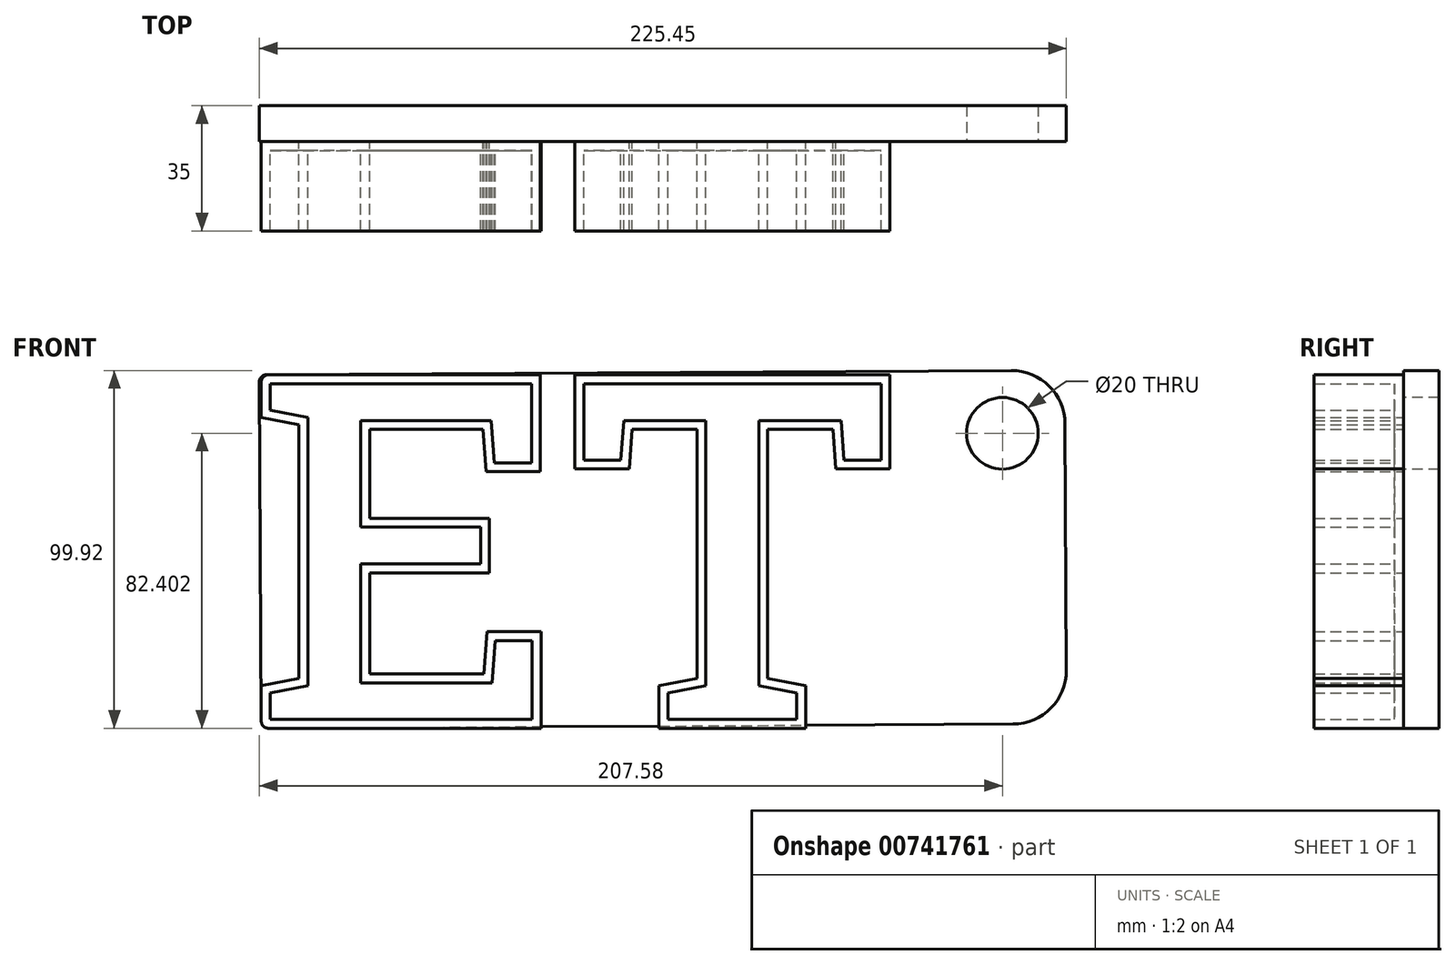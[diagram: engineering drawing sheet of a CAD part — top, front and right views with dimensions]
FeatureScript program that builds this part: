
annotation { "Feature Type Name" : "Feature", "Feature Type Description" : "" }
export const myFeature = defineFeature(function(context is Context, id is Id, definition is map)
    precondition{}
    {
        {
            var Q0;
            Q0=qCreatedBy(makeId("Front.planeOp"),FACE);
            var sketch = newSketch(context, id + "F0", { "sketchPlane" : qUnion([Q0])});
            skText(sketch, "E0", { "text": "ET", "fontName": "RobotoSlab-Bold.ttf"});
            const initialGuessF0  = {"E0": [0, -0.1, 1, 0, 0.1]};
            skSetInitialGuess(sketch, initialGuessF0);
            skSolve(sketch);
        }
        {
            var Q0;
            Q0 = qSketchRegion(id + "F0", true);
            extrude(context, id + "F1", {"entities" : qUnion([Q0]), "depth" : 25 * mm, "offsetDistance" : 25 * mm});
        }
        {
            var Q0;
            Q0=makeQuery(id+"F1.opExtrude","CAP_FACE",FACE,{"disambiguationData":[OSD([sQuery(id+"F0.wireOp",EDGE,"E0.sketch_text.stroke-0"),sQuery(id+"F0.wireOp",EDGE,"E0.sketch_text.stroke-1"),sQuery(id+"F0.wireOp",EDGE,"E0.sketch_text.stroke-2"),sQuery(id+"F0.wireOp",EDGE,"E0.sketch_text.stroke-3"),sQuery(id+"F0.wireOp",EDGE,"E0.sketch_text.stroke-4"),sQuery(id+"F0.wireOp",EDGE,"E0.sketch_text.stroke-5"),sQuery(id+"F0.wireOp",EDGE,"E0.sketch_text.stroke-6"),sQuery(id+"F0.wireOp",EDGE,"E0.sketch_text.stroke-7"),sQuery(id+"F0.wireOp",EDGE,"E0.sketch_text.stroke-8"),sQuery(id+"F0.wireOp",EDGE,"E0.sketch_text.stroke-9"),sQuery(id+"F0.wireOp",EDGE,"E0.sketch_text.stroke-10"),sQuery(id+"F0.wireOp",EDGE,"E0.sketch_text.stroke-11"),sQuery(id+"F0.wireOp",EDGE,"E0.sketch_text.stroke-12"),sQuery(id+"F0.wireOp",EDGE,"E0.sketch_text.stroke-13"),sQuery(id+"F0.wireOp",EDGE,"E0.sketch_text.stroke-14"),sQuery(id+"F0.wireOp",EDGE,"E0.sketch_text.stroke-15"),sQuery(id+"F0.wireOp",EDGE,"E0.sketch_text.stroke-16"),sQuery(id+"F0.wireOp",EDGE,"E0.sketch_text.stroke-17"),sQuery(id+"F0.wireOp",EDGE,"E0.sketch_text.stroke-18"),sQuery(id+"F0.wireOp",EDGE,"E0.sketch_text.stroke-19"),sQuery(id+"F0.wireOp",EDGE,"E0.sketch_text.stroke-20")])],"isStart":false});
            var Q1;
            Q1=makeQuery(id+"F1.opExtrude","CAP_FACE",FACE,{"disambiguationData":[OSD([sQuery(id+"F0.wireOp",EDGE,"E0.sketch_text.stroke-21"),sQuery(id+"F0.wireOp",EDGE,"E0.sketch_text.stroke-22"),sQuery(id+"F0.wireOp",EDGE,"E0.sketch_text.stroke-23"),sQuery(id+"F0.wireOp",EDGE,"E0.sketch_text.stroke-24"),sQuery(id+"F0.wireOp",EDGE,"E0.sketch_text.stroke-25"),sQuery(id+"F0.wireOp",EDGE,"E0.sketch_text.stroke-26"),sQuery(id+"F0.wireOp",EDGE,"E0.sketch_text.stroke-27"),sQuery(id+"F0.wireOp",EDGE,"E0.sketch_text.stroke-28"),sQuery(id+"F0.wireOp",EDGE,"E0.sketch_text.stroke-29"),sQuery(id+"F0.wireOp",EDGE,"E0.sketch_text.stroke-30"),sQuery(id+"F0.wireOp",EDGE,"E0.sketch_text.stroke-31"),sQuery(id+"F0.wireOp",EDGE,"E0.sketch_text.stroke-32"),sQuery(id+"F0.wireOp",EDGE,"E0.sketch_text.stroke-33"),sQuery(id+"F0.wireOp",EDGE,"E0.sketch_text.stroke-34"),sQuery(id+"F0.wireOp",EDGE,"E0.sketch_text.stroke-35"),sQuery(id+"F0.wireOp",EDGE,"E0.sketch_text.stroke-36")])],"isStart":false});
            shell(context, id + "F2", {"entities" : qUnion([Q0, Q1]), "thickness" : 2.5 * mm});
        }
        {
            var Q0;
            Q0=makeQuery(id+"F1.opExtrude","CAP_FACE",FACE,{"disambiguationData":[OSD([sQuery(id+"F0.wireOp",EDGE,"E0.sketch_text.stroke-0"),sQuery(id+"F0.wireOp",EDGE,"E0.sketch_text.stroke-1"),sQuery(id+"F0.wireOp",EDGE,"E0.sketch_text.stroke-2"),sQuery(id+"F0.wireOp",EDGE,"E0.sketch_text.stroke-3"),sQuery(id+"F0.wireOp",EDGE,"E0.sketch_text.stroke-4"),sQuery(id+"F0.wireOp",EDGE,"E0.sketch_text.stroke-5"),sQuery(id+"F0.wireOp",EDGE,"E0.sketch_text.stroke-6"),sQuery(id+"F0.wireOp",EDGE,"E0.sketch_text.stroke-7"),sQuery(id+"F0.wireOp",EDGE,"E0.sketch_text.stroke-8"),sQuery(id+"F0.wireOp",EDGE,"E0.sketch_text.stroke-9"),sQuery(id+"F0.wireOp",EDGE,"E0.sketch_text.stroke-10"),sQuery(id+"F0.wireOp",EDGE,"E0.sketch_text.stroke-11"),sQuery(id+"F0.wireOp",EDGE,"E0.sketch_text.stroke-12"),sQuery(id+"F0.wireOp",EDGE,"E0.sketch_text.stroke-13"),sQuery(id+"F0.wireOp",EDGE,"E0.sketch_text.stroke-14"),sQuery(id+"F0.wireOp",EDGE,"E0.sketch_text.stroke-15"),sQuery(id+"F0.wireOp",EDGE,"E0.sketch_text.stroke-16"),sQuery(id+"F0.wireOp",EDGE,"E0.sketch_text.stroke-17"),sQuery(id+"F0.wireOp",EDGE,"E0.sketch_text.stroke-18"),sQuery(id+"F0.wireOp",EDGE,"E0.sketch_text.stroke-19"),sQuery(id+"F0.wireOp",EDGE,"E0.sketch_text.stroke-20")])],"isStart":true});
            var sketch = newSketch(context, id + "F3", { "sketchPlane" : qUnion([Q0])});
            skLineSegment(sketch, "E1.bottom", {"start": v(-3.8, -100) * mm, "end": v(-228.8, -98.74) * mm});
            skLineSegment(sketch, "E1.top", {"start": v(-3.25, -1.26) * mm, "end": v(-228.24, 0) * mm});
            skLineSegment(sketch, "E1.left", {"start": v(-3.8, -100) * mm, "end": v(-3.25, -1.26) * mm});
            skLineSegment(sketch, "E1.right", {"start": v(-228.8, -98.74) * mm, "end": v(-228.24, 0) * mm});
            skSolve(sketch);
        }
        {
            var Q0;
            Q0 = qSketchRegion(id + "F3", true);
            extrude(context, id + "F4", {"entities" : qUnion([Q0]), "depth" : 10 * mm, "offsetDistance" : 25 * mm});
        }
        {
            var Q0;
            Q0=makeQuery(id+"F4.opExtrude","CAP_FACE",FACE,{"disambiguationData":[OSD([sQuery(id+"F3.wireOp",EDGE,"E1.bottom"),sQuery(id+"F3.wireOp",EDGE,"E1.top"),sQuery(id+"F3.wireOp",EDGE,"E1.left"),sQuery(id+"F3.wireOp",EDGE,"E1.right")])],"isStart":true});
            var sketch = newSketch(context, id + "F5", { "sketchPlane" : qUnion([Q0])});
            skPoint(sketch, "E2", {"position": v(210.84, -17.6) * mm});
            skSolve(sketch);
        }
        {
            var Q0;
            Q0=sQuery(id+"F5.wireOp",VERTEX,"E2");
            var Q1;
            Q1=makeQuery(id+"F4.opExtrude","SWEPT_BODY",BODY,{"disambiguationData":[OSD([sQuery(id+"F3.wireOp",EDGE,"E1.bottom"),sQuery(id+"F3.wireOp",EDGE,"E1.top"),sQuery(id+"F3.wireOp",EDGE,"E1.left"),sQuery(id+"F3.wireOp",EDGE,"E1.right")])]});
            hole(context, id + "F6", {"style" : HoleStyle.SIMPLE, "endStyle" : HoleEndStyle.THROUGH, "holeDiameter" : 20 * mm, "majorDiameter" : 5 * mm, "isTappedThrough" : true, "tappedDepth" : 12 * mm, "tapClearance" : 3, "locations" : qUnion([Q0]), "scope" : qUnion([Q1])});
        }
        {
            var Q0;
            Q0=makeQuery(id+"F4.opExtrude","SWEPT_EDGE",EDGE,{"disambiguationData":[OSD([sQuery(id+"F3.wireOp",EDGE,"E1.top"),sQuery(id+"F3.wireOp",EDGE,"E1.right")])]});
            var Q1;
            Q1=makeQuery(id+"F4.opExtrude","SWEPT_EDGE",EDGE,{"disambiguationData":[OSD([sQuery(id+"F3.wireOp",EDGE,"E1.bottom"),sQuery(id+"F3.wireOp",EDGE,"E1.right")])]});
            fillet(context, id + "F7", {"entities" : qUnion([Q0, Q1]), "radius" : 15 * mm, "tangentPropagation" : true, "allowEdgeOverflow" : false});
        }
        {
            var Q0;
            Q0=makeQuery(id+"F4.opExtrude","SWEPT_EDGE",EDGE,{"disambiguationData":[OSD([sQuery(id+"F3.wireOp",EDGE,"E1.bottom"),sQuery(id+"F3.wireOp",EDGE,"E1.left")])]});
            var Q1;
            Q1=makeQuery(id+"F1.opExtrude","SWEPT_EDGE",EDGE,{"disambiguationData":[OSD([sQuery(id+"F0.wireOp",EDGE,"E0.sketch_text.stroke-6"),sQuery(id+"F0.wireOp",EDGE,"E0.sketch_text.stroke-7")])]});
            var Q2;
            Q2=makeQuery(id+"F4.opExtrude","SWEPT_EDGE",EDGE,{"disambiguationData":[OSD([sQuery(id+"F3.wireOp",EDGE,"E1.top"),sQuery(id+"F3.wireOp",EDGE,"E1.left")])]});
            var Q3;
            Q3=makeQuery(id+"F1.opExtrude","SWEPT_EDGE",EDGE,{"disambiguationData":[OSD([sQuery(id+"F0.wireOp",EDGE,"E0.sketch_text.stroke-11"),sQuery(id+"F0.wireOp",EDGE,"E0.sketch_text.stroke-12")])]});
            fillet(context, id + "F8", {"entities" : qUnion([Q0, Q1, Q2, Q3]), "radius" : 2 * mm, "tangentPropagation" : true, "allowEdgeOverflow" : false});
        }
    });
